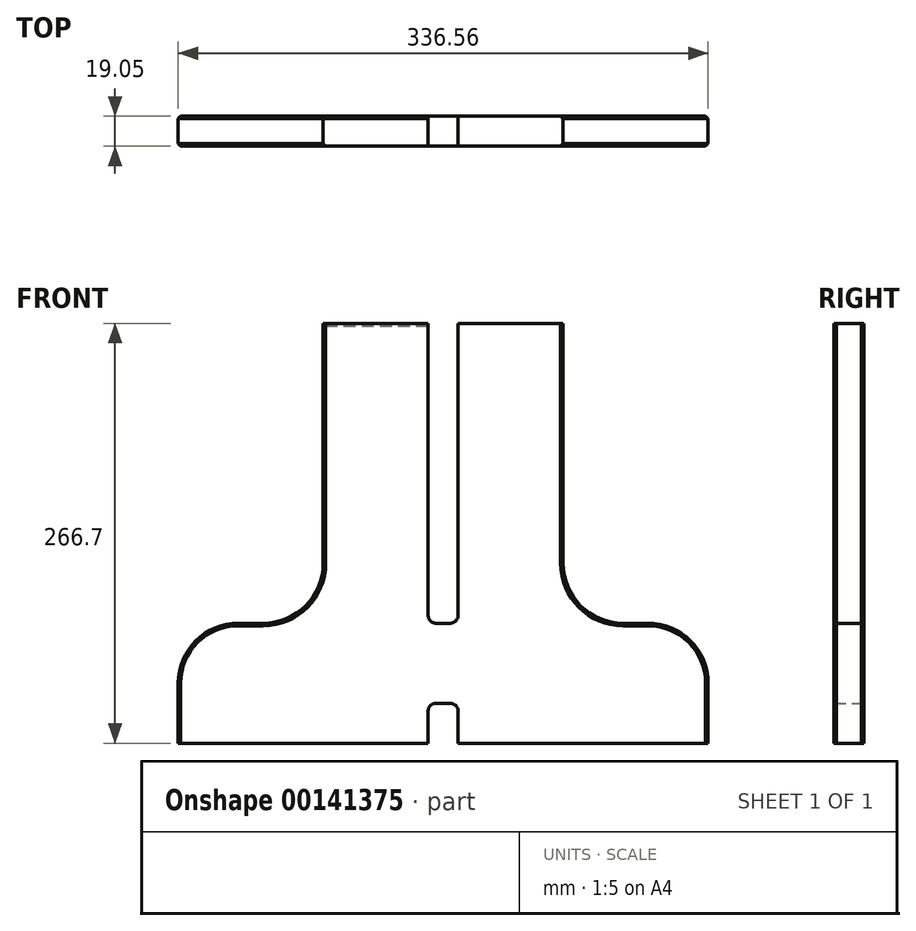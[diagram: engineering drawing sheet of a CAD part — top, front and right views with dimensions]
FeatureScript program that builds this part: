
annotation { "Feature Type Name" : "Feature", "Feature Type Description" : "" }
export const myFeature = defineFeature(function(context is Context, id is Id, definition is map)
    precondition{}
    {
        {
            var Q0;
            Q0=qCreatedBy(makeId("Front.planeOp"),FACE);
            var sketch = newSketch(context, id + "F0", { "sketchPlane" : qUnion([Q0])});
            skLineSegment(sketch, "E0.left", {"start": v(76.2, 95.25) * mm, "end": v(76.2, -95.25) * mm});
            skLineSegment(sketch, "E0.right", {"start": v(-76.2, 95.25) * mm, "end": v(-76.2, -95.25) * mm});
            skPoint(sketch, "E0.middle", {"position": v(0, 0) * mm});
            skLineSegment(sketch, "E1", {"start": v(-168.28, -171.45) * mm, "end": v(-168.28, -95.25) * mm});
            skLineSegment(sketch, "E2", {"start": v(-168.28, -95.25) * mm, "end": v(-76.2, -95.25) * mm});
            skLineSegment(sketch, "E3", {"start": v(168.28, -171.45) * mm, "end": v(168.28, -95.25) * mm});
            skLineSegment(sketch, "E4", {"start": v(168.28, -95.25) * mm, "end": v(76.2, -95.25) * mm});
            skLineSegment(sketch, "E5", {"start": v(-9.53, -95.25) * mm, "end": v(9.52, -95.25) * mm});
            skLineSegment(sketch, "E6", {"start": v(-76.2, 95.25) * mm, "end": v(-9.53, 95.25) * mm});
            skLineSegment(sketch, "E7", {"start": v(-9.53, 95.25) * mm, "end": v(-9.53, -95.25) * mm});
            skLineSegment(sketch, "E8", {"start": v(9.52, -95.25) * mm, "end": v(9.52, 95.25) * mm});
            skLineSegment(sketch, "E9", {"start": v(9.52, 95.25) * mm, "end": v(76.2, 95.25) * mm});
            skLineSegment(sketch, "E10", {"start": v(-9.52, -171.45) * mm, "end": v(-9.52, -146.05) * mm});
            skLineSegment(sketch, "E11", {"start": v(-9.52, -146.05) * mm, "end": v(9.53, -146.05) * mm});
            skLineSegment(sketch, "E12", {"start": v(9.53, -146.05) * mm, "end": v(9.53, -171.45) * mm});
            skLineSegment(sketch, "E13", {"start": v(168.28, -171.45) * mm, "end": v(9.53, -171.45) * mm});
            skLineSegment(sketch, "E14", {"start": v(-9.53, -171.45) * mm, "end": v(-168.28, -171.45) * mm});
            skSolve(sketch);
        }
        {
            var Q0;
            Q0=makeQuery(id+"F0.imprint","IMPRINT",FACE,{"disambiguationData":[TD([[makeQuery(id+"F0.imprint","IMPRINT",EDGE,{"derivedFrom":sQuery(id+"F0.wireOp",EDGE,"E0.left")}),-1.0]])]});
            extrude(context, id + "F1", {"entities" : qUnion([Q0]), "depth" : 19.05 * mm});
        }
        {
            var Q0;
            Q0=makeQuery(id+"F1.opExtrude","SWEPT_EDGE",EDGE,{"disambiguationData":[OSD([sQuery(id+"F0.wireOp",EDGE,"E1"),sQuery(id+"F0.wireOp",EDGE,"E2")])]});
            var Q1;
            Q1=makeQuery(id+"F1.opExtrude","SWEPT_EDGE",EDGE,{"disambiguationData":[OSD([sQuery(id+"F0.wireOp",EDGE,"E0.right"),sQuery(id+"F0.wireOp",EDGE,"E2")])]});
            var Q2;
            Q2=makeQuery(id+"F1.opExtrude","SWEPT_EDGE",EDGE,{"disambiguationData":[OSD([sQuery(id+"F0.wireOp",EDGE,"E0.left"),sQuery(id+"F0.wireOp",EDGE,"E4")])]});
            var Q3;
            Q3=makeQuery(id+"F1.opExtrude","SWEPT_EDGE",EDGE,{"disambiguationData":[OSD([sQuery(id+"F0.wireOp",EDGE,"E3"),sQuery(id+"F0.wireOp",EDGE,"E4")])]});
            fillet(context, id + "F2", {"entities" : qUnion([Q0, Q1, Q2, Q3]), "radius" : 38.1 * mm, "tangentPropagation" : true, "allowEdgeOverflow" : false});
        }
        {
            var Q0;
            Q0=makeQuery(id+"F1.opExtrude","SWEPT_EDGE",EDGE,{"disambiguationData":[OSD([sQuery(id+"F0.wireOp",EDGE,"E5"),sQuery(id+"F0.wireOp",EDGE,"E8")])]});
            var Q1;
            Q1=makeQuery(id+"F1.opExtrude","SWEPT_EDGE",EDGE,{"disambiguationData":[OSD([sQuery(id+"F0.wireOp",EDGE,"E5"),sQuery(id+"F0.wireOp",EDGE,"E7")])]});
            var Q2;
            Q2=makeQuery(id+"F1.opExtrude","SWEPT_EDGE",EDGE,{"disambiguationData":[OSD([sQuery(id+"F0.wireOp",EDGE,"E10"),sQuery(id+"F0.wireOp",EDGE,"E11")])]});
            var Q3;
            Q3=makeQuery(id+"F1.opExtrude","SWEPT_EDGE",EDGE,{"disambiguationData":[OSD([sQuery(id+"F0.wireOp",EDGE,"E11"),sQuery(id+"F0.wireOp",EDGE,"E12")])]});
            fillet(context, id + "F3", {"entities" : qUnion([Q0, Q1, Q2, Q3]), "radius" : 5.08 * mm, "tangentPropagation" : true, "allowEdgeOverflow" : false});
        }
        {
            var Q0;
            Q0=makeQuery(id+"F1.opExtrude","CAP_EDGE",EDGE,{"disambiguationData":[OSD([sQuery(id+"F0.wireOp",EDGE,"E2")])],"isStart":false});
            var Q1;
            Q1=makeQuery(id+"F1.opExtrude","CAP_EDGE",EDGE,{"disambiguationData":[OSD([sQuery(id+"F0.wireOp",EDGE,"E4")])],"isStart":false});
            var Q2;
            Q2=makeQuery(id+"F1.opExtrude","CAP_EDGE",EDGE,{"disambiguationData":[OSD([sQuery(id+"F0.wireOp",EDGE,"E4")])],"isStart":true});
            var Q3;
            Q3=makeQuery(id+"F1.opExtrude","CAP_EDGE",EDGE,{"disambiguationData":[OSD([sQuery(id+"F0.wireOp",EDGE,"E6")])],"isStart":true});
            var Q4;
            Q4=makeQuery(id+"F1.opExtrude","CAP_EDGE",EDGE,{"disambiguationData":[OSD([sQuery(id+"F0.wireOp",EDGE,"E0.right")])],"isStart":true});
            var Q5;
            Q5=makeQuery(id+"F1.opExtrude","CAP_EDGE",EDGE,{"disambiguationData":[OSD([sQuery(id+"F0.wireOp",EDGE,"E2")])],"isStart":true});
            chamfer(context, id + "F4", {"entities" : qUnion([Q0, Q1, Q2, Q3, Q4, Q5]), "width" : 1.59 * mm, "tangentPropagation" : true});
        }
    });
